# Revit family: PRD_AR_JntrlUnits_SiriusMultiPurposeSink_BS351,BS352
name_source: partatom
category: Plumbing Fixtures
revit_build: Autodesk Revit 2018 (Build: 20190510_1515(x64)
units: mm (PartAtom-declared; Revit-internal decimal feet)

## family parameters
Always vertical = Yes
Cut with Voids When Loaded = No
OmniClass Number = 23.45.05.14.14
OmniClass Title = Sinks/Lavatories
Part Type = Normal
Room Calculation Point = No
Round Connector Dimension = Use Diameter
Shared = No
Work Plane-Based = No

## types (2) — shared parameters
AssetType = Fixed
Category = Pr_40_20_96_44, Janitorial sinks
Color = Stainless steel
DrainSize = DN 40 (1 1/2 inch.)
DurationUnit = year
Features = stainless steel, 1.20 mm, satin finished, various types, 1100x357x550 mm (WxHxD)
Finish = Satin finished
FinishAndMaterial = Stainless steel 1.4301
Form = Stainless steel multi purpose sink
GrossWeight = 36.00 kg
IfcExportAs = IfcSanitaryTerminalType
IfcExportType = SINK
IntegralAccessories = incl. waste kit
Manufacturer = KWC Group AG
ManufacturerName = KWC Group AG
ManufacturerURL = www.kwc.com
Material = Stainless steel
NBSDescription = Janitorial units
NBSReference = 45-35-70/401
NetWeight = 13.00 kg
NominalDepth = 550 mm  [stored 1.80446 ft]
NominalHeight = 357 mm  [stored 1.17126 ft]
NominalWidth = 1100 mm
ProductInformation = https://pim.kwc.com
Shape = Rectangular
SinkMaterial = PRD_AR_StainlessSteel_SatinFinished
SinkMounting = Other
SinkType = Other
Size = 1100 x 550 x 357 mm
URL = www.kwc.com
Uniclass2015Code = Pr_40_20_96_44
Uniclass2015Title = Janitorial sinks
Uniclass2015Version = Products v1.10
Version = 1
WarrantyDurationUnit = year
WasteSize = 40  [stored 0.131234 ft]
WaterSupplyOverflowAndWasteHolesOverflow = Stand pipe overflow
WaterSupplyOverflowAndWasteHolesWaterSupply = No tapholes

## per-type parameters (varying)
| type | BIMObjectName | Description | Left | ModelNumber | Name | Right | WaterSupplyOverflowAndWasteHolesWaste |
| BS351 | PRD_AR_JanitorialUnits_SiriusMultiPurposeSink_BS351 | General purpose sink for inset or wall mounting, stainless steel, surface satin finished, material thickness 1.2 mm, deep drawn seamless welded bowl, 1 1/2'' waste with standpipe strainer, drain board with riffle, 40 mm rear upstand, wall mounting brackets optional. one bowl, drainboard left, width 1100 mm | Yes | 2000100062 | Sirius multi purpose sink BS351 | No | Left-Back-Corner |
| BS352 | PRD_AR_JanitorialUnits_SiriusMultiPurposeSink_BS352 | General purpose sink for inset or wall mounting, stainless steel, surface satin finished, material thickness 1.2 mm, deep drawn seamless welded bowl, 1 1/2'' waste with standpipe strainer, drain board with riffle, 40 mm rear upstand, wall mounting brackets optional. one bowl, drain board right, width 1100 mm | No | 2000100063 | Sirius multi purpose sink BS352 | Yes | Right-Back-Corner |

note: column(s) folded — value = type name in every type: Model, ModelReference

note: [stored X ft] marks values corroborated as IEEE doubles in the binary element streams (Revit-internal decimal feet)

## geometry (parser evidence)
native form markers: Sweep x8
no freeform markers — native parametric forms only
